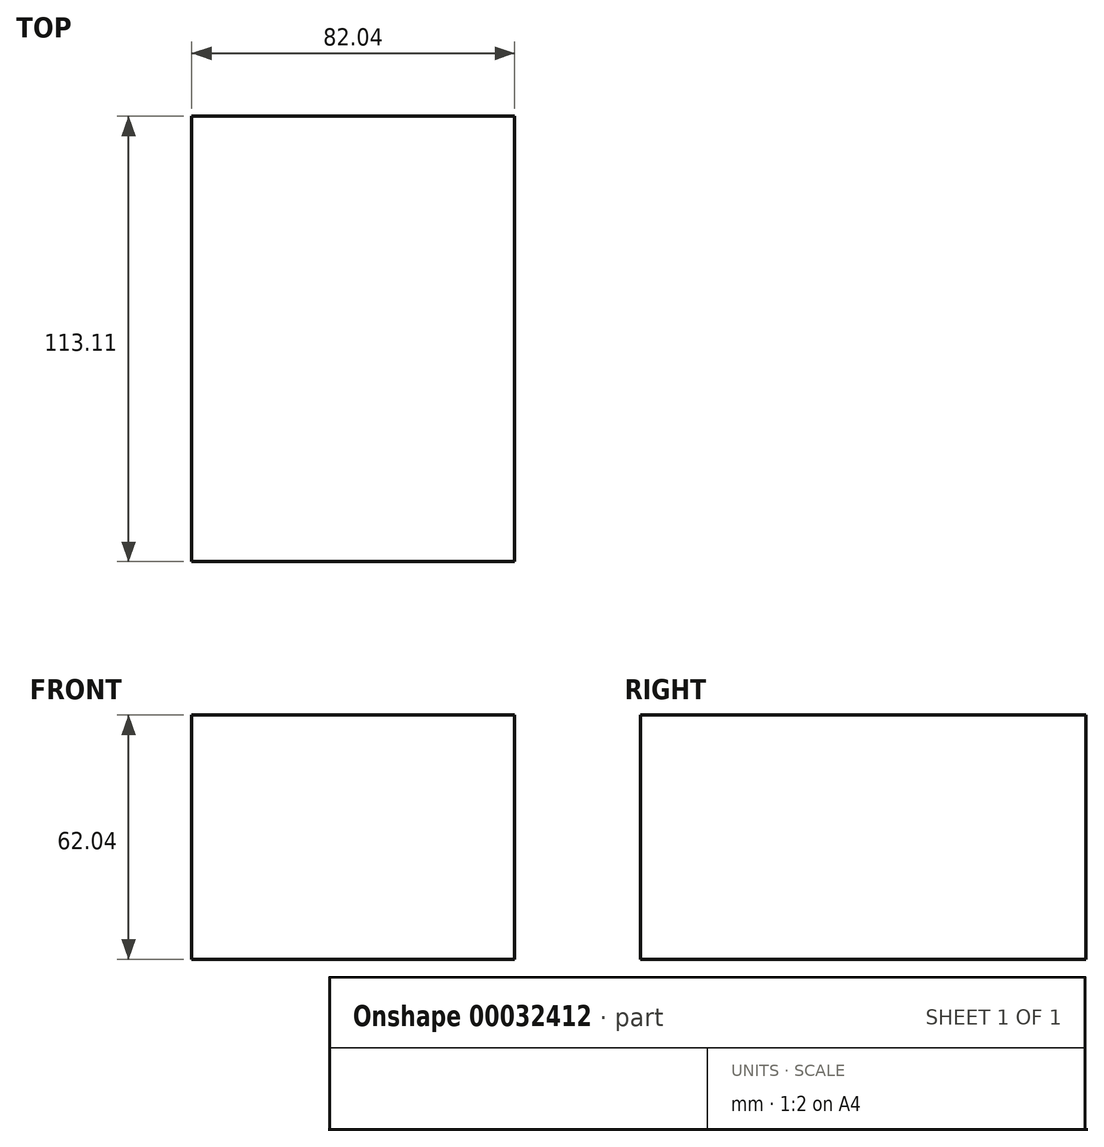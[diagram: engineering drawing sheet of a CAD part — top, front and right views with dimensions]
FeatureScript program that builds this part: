
annotation { "Feature Type Name" : "Feature", "Feature Type Description" : "" }
export const myFeature = defineFeature(function(context is Context, id is Id, definition is map)
    precondition{}
    {
        {
            var Q0;
            Q0=qCreatedBy(makeId("Front.planeOp"),FACE);
            var sketch = newSketch(context, id + "F0", { "sketchPlane" : qUnion([Q0])});
            skLineSegment(sketch, "E0.rect.bottom", {"start": v(41.02, -31.02) * mm, "end": v(-41.02, -31.02) * mm});
            skLineSegment(sketch, "E0.rect.top", {"start": v(41.02, 31.02) * mm, "end": v(-41.02, 31.02) * mm});
            skLineSegment(sketch, "E0.rect.left", {"start": v(41.02, -31.02) * mm, "end": v(41.02, 31.02) * mm});
            skLineSegment(sketch, "E0.rect.right", {"start": v(-41.02, -31.02) * mm, "end": v(-41.02, 31.02) * mm});
            skPoint(sketch, "E0.rect.middle", {"position": v(0, 0) * mm});
            skSolve(sketch);
        }
        {
            var Q0;
            Q0=makeQuery(id+"F0.imprint","IMPRINT",FACE,{"disambiguationData":[TD([[makeQuery(id+"F0.imprint","IMPRINT",EDGE,{"derivedFrom":sQuery(id+"F0.wireOp",EDGE,"E0.rect.bottom")}),-1.0]])]});
            extrude(context, id + "F1", {"entities" : qUnion([Q0]), "depth" : 113.11 * mm});
        }
    });
